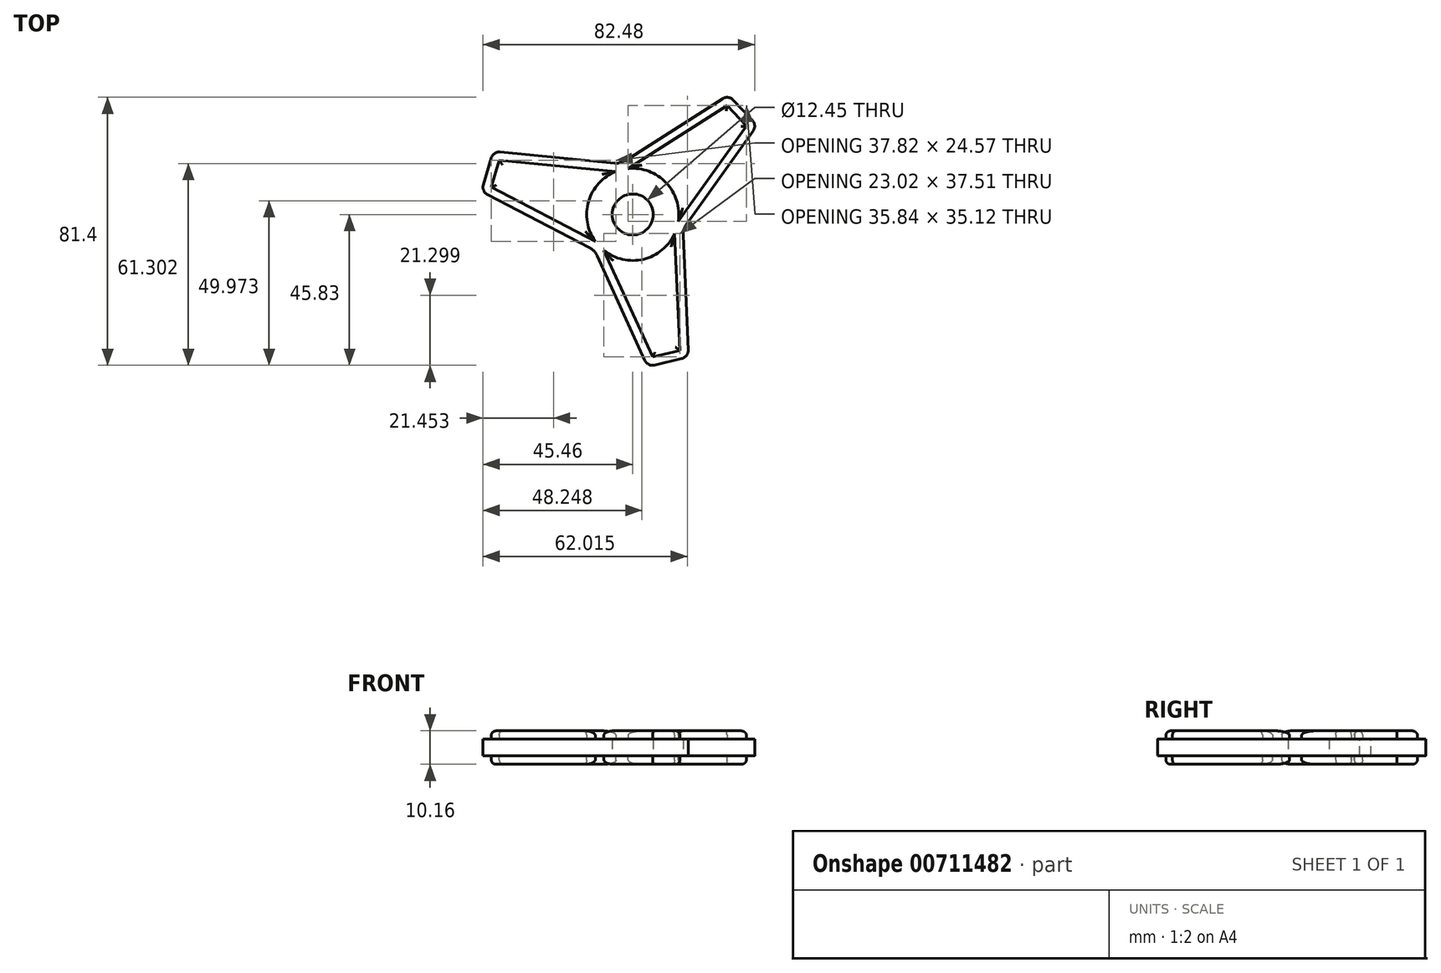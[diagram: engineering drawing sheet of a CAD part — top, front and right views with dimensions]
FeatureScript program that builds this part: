
annotation { "Feature Type Name" : "Feature", "Feature Type Description" : "" }
export const myFeature = defineFeature(function(context is Context, id is Id, definition is map)
    precondition{}
    {
        {
            var Q0;
            Q0=qCreatedBy(makeId("Top.planeOp"),FACE);
            var sketch = newSketch(context, id + "F0", { "sketchPlane" : qUnion([Q0])});
            skCircle(sketch, "E0", {"center": v(0, 0) * mm, "radius": 6.22 * mm});
            skCircle(sketch, "E1", {"center": v(0, 0) * mm, "radius": 15.88 * mm});
            skCircle(sketch, "E2.cCircle", {"center": v(0, 0) * mm, "radius": 15.88 * mm, "construction": true});
            skLineSegment(sketch, "E2.0", {"start": v(-11.51, -10.93) * mm, "end": v(-3.7, 15.44) * mm});
            skLineSegment(sketch, "E2.1", {"start": v(-3.7, 15.44) * mm, "end": v(15.22, -4.5) * mm});
            skLineSegment(sketch, "E2.2", {"start": v(15.22, -4.5) * mm, "end": v(-11.51, -10.93) * mm});
            skLineSegment(sketch, "E3", {"start": v(15.22, -4.5) * mm, "end": v(1.85, -7.72) * mm});
            skLineSegment(sketch, "E4", {"start": v(1.85, -7.72) * mm, "end": v(10.75, -44.76) * mm});
            skLineSegment(sketch, "E5", {"start": v(10.75, -44.76) * mm, "end": v(16.93, -43.28) * mm});
            skLineSegment(sketch, "E6", {"start": v(16.93, -43.28) * mm, "end": v(4.58, -46.25) * mm});
            skLineSegment(sketch, "E7", {"start": v(16.93, -43.28) * mm, "end": v(15.22, -4.5) * mm});
            skLineSegment(sketch, "E8", {"start": v(-11.51, -10.93) * mm, "end": v(4.58, -46.25) * mm});
            skLineSegment(sketch, "E9", {"start": v(15.22, -4.5) * mm, "end": v(5.76, 5.46) * mm});
            skLineSegment(sketch, "E10", {"start": v(5.76, 5.46) * mm, "end": v(33.39, 31.7) * mm});
            skLineSegment(sketch, "E11", {"start": v(33.39, 31.7) * mm, "end": v(29.02, 36.3) * mm});
            skLineSegment(sketch, "E12", {"start": v(33.39, 31.7) * mm, "end": v(37.76, 27.09) * mm});
            skLineSegment(sketch, "E13", {"start": v(37.76, 27.09) * mm, "end": v(15.22, -4.5) * mm});
            skLineSegment(sketch, "E14", {"start": v(-3.7, 15.44) * mm, "end": v(29.02, 36.3) * mm});
            skLineSegment(sketch, "E15", {"start": v(-7.61, 2.25) * mm, "end": v(-44.14, 13.07) * mm});
            skLineSegment(sketch, "E16", {"start": v(-44.14, 13.07) * mm, "end": v(-42.34, 19.16) * mm});
            skLineSegment(sketch, "E17", {"start": v(-44.14, 13.07) * mm, "end": v(-45.95, 6.98) * mm});
            skLineSegment(sketch, "E18", {"start": v(-11.51, -10.93) * mm, "end": v(-45.95, 6.98) * mm});
            skLineSegment(sketch, "E19", {"start": v(-42.34, 19.16) * mm, "end": v(-3.7, 15.44) * mm});
            skSolve(sketch);
        }
        {
            var Q0;
            {var subQ4=sQuery(id+"F0.wireOp",EDGE,"E17");Q0=makeQuery(id+"F0.imprint","IMPRINT",FACE,{"disambiguationData":[TD([[makeQuery(id+"F0.imprint","IMPRINT",EDGE,{"derivedFrom":subQ4}),1.0]])]});}
            var Q1;
            {var subQ4=sQuery(id+"F0.wireOp",EDGE,"E16");Q1=makeQuery(id+"F0.imprint","IMPRINT",FACE,{"disambiguationData":[TD([[makeQuery(id+"F0.imprint","IMPRINT",EDGE,{"derivedFrom":subQ4}),-1.0]])]});}
            var Q2;
            {var subQ0=sQuery(id+"F0.wireOp",EDGE,"E2.0");var subQ3=sQuery(id+"F0.wireOp",EDGE,"E15");var subQ5=makeQuery(id+"F0.imprint","INTERSECT",VERTEX,{"derivedFrom":[subQ0,subQ3]});Q2=makeQuery(id+"F0.imprint","IMPRINT",FACE,{"disambiguationData":[TD([[makeQuery(id+"F0.imprint","IMPRINT",EDGE,{"disambiguationData":[TD([[subQ5,-1.0]])],"derivedFrom":subQ3}),1.0]])]});}
            var Q3;
            {var subQ0=sQuery(id+"F0.wireOp",EDGE,"E2.0");var subQ3=sQuery(id+"F0.wireOp",EDGE,"E15");var subQ5=makeQuery(id+"F0.imprint","INTERSECT",VERTEX,{"derivedFrom":[subQ0,subQ3]});Q3=makeQuery(id+"F0.imprint","IMPRINT",FACE,{"disambiguationData":[TD([[makeQuery(id+"F0.imprint","IMPRINT",EDGE,{"disambiguationData":[TD([[subQ5,-1.0]])],"derivedFrom":subQ3}),-1.0]])]});}
            var Q4;
            Q4=makeQuery(id+"F0.imprint","IMPRINT",FACE,{"disambiguationData":[TD([[makeQuery(id+"F0.imprint","IMPRINT",EDGE,{"derivedFrom":sQuery(id+"F0.wireOp",EDGE,"E0")}),-1.0]])]});
            var Q5;
            {var subQ0=sQuery(id+"F0.wireOp",EDGE,"E2.1");Q5=makeQuery(id+"F0.imprint","IMPRINT",FACE,{"disambiguationData":[TD([[makeQuery(id+"F0.imprint","IMPRINT",EDGE,{"derivedFrom":subQ0}),1.0]])]});}
            var Q6;
            {var subQ4=sQuery(id+"F0.wireOp",EDGE,"E12");Q6=makeQuery(id+"F0.imprint","IMPRINT",FACE,{"disambiguationData":[TD([[makeQuery(id+"F0.imprint","IMPRINT",EDGE,{"derivedFrom":subQ4}),-1.0]])]});}
            var Q7;
            {var subQ4=sQuery(id+"F0.wireOp",EDGE,"E11");Q7=makeQuery(id+"F0.imprint","IMPRINT",FACE,{"disambiguationData":[TD([[makeQuery(id+"F0.imprint","IMPRINT",EDGE,{"derivedFrom":subQ4}),1.0]])]});}
            var Q8;
            {var subQ0=sQuery(id+"F0.wireOp",EDGE,"E3");Q8=makeQuery(id+"F0.imprint","IMPRINT",FACE,{"disambiguationData":[TD([[makeQuery(id+"F0.imprint","IMPRINT",EDGE,{"derivedFrom":subQ0}),1.0]])]});}
            var Q9;
            {var subQ0=sQuery(id+"F0.wireOp",EDGE,"E2.2");Q9=makeQuery(id+"F0.imprint","IMPRINT",FACE,{"disambiguationData":[TD([[makeQuery(id+"F0.imprint","IMPRINT",EDGE,{"derivedFrom":subQ0}),1.0]])]});}
            var Q10;
            {var subQ0=sQuery(id+"F0.wireOp",EDGE,"E8");Q10=makeQuery(id+"F0.imprint","IMPRINT",FACE,{"disambiguationData":[TD([[makeQuery(id+"F0.imprint","IMPRINT",EDGE,{"derivedFrom":subQ0}),1.0]])]});}
            var Q11;
            {var subQ0=sQuery(id+"F0.wireOp",EDGE,"E7");Q11=makeQuery(id+"F0.imprint","IMPRINT",FACE,{"disambiguationData":[TD([[makeQuery(id+"F0.imprint","IMPRINT",EDGE,{"derivedFrom":subQ0}),1.0]])]});}
            var Q12;
            {var subQ0=sQuery(id+"F0.wireOp",EDGE,"E9");Q12=makeQuery(id+"F0.imprint","IMPRINT",FACE,{"disambiguationData":[TD([[makeQuery(id+"F0.imprint","IMPRINT",EDGE,{"derivedFrom":subQ0}),-1.0]])]});}
            extrude(context, id + "F1", {"entities" : qUnion([Q0, Q1, Q2, Q3, Q4, Q5, Q6, Q7, Q8, Q9, Q10, Q11, Q12]), "depth" : 5.08 * mm, "offsetDistance" : 25.4 * mm});
        }
        {
            var Q0;
            Q0=makeQuery(id+"F1.opExtrude","SWEPT_EDGE",EDGE,{"disambiguationData":[OSD([sQuery(id+"F0.wireOp",EDGE,"E17"),sQuery(id+"F0.wireOp",EDGE,"E18")])]});
            var Q1;
            Q1=makeQuery(id+"F1.opExtrude","SWEPT_EDGE",EDGE,{"disambiguationData":[OSD([sQuery(id+"F0.wireOp",EDGE,"E16"),sQuery(id+"F0.wireOp",EDGE,"E19")])]});
            var Q2;
            Q2=makeQuery(id+"F1.opExtrude","SWEPT_EDGE",EDGE,{"disambiguationData":[OSD([sQuery(id+"F0.wireOp",EDGE,"E11"),sQuery(id+"F0.wireOp",EDGE,"E14")])]});
            var Q3;
            Q3=makeQuery(id+"F1.opExtrude","SWEPT_EDGE",EDGE,{"disambiguationData":[OSD([sQuery(id+"F0.wireOp",EDGE,"E12"),sQuery(id+"F0.wireOp",EDGE,"E13")])]});
            var Q4;
            Q4=makeQuery(id+"F1.opExtrude","SWEPT_EDGE",EDGE,{"disambiguationData":[OSD([sQuery(id+"F0.wireOp",EDGE,"E6"),sQuery(id+"F0.wireOp",EDGE,"E7")])]});
            var Q5;
            Q5=makeQuery(id+"F1.opExtrude","SWEPT_EDGE",EDGE,{"disambiguationData":[OSD([sQuery(id+"F0.wireOp",EDGE,"E6"),sQuery(id+"F0.wireOp",EDGE,"E8")])]});
            fillet(context, id + "F2", {"entities" : qUnion([Q0, Q1, Q2, Q3, Q4, Q5]), "radius" : 2.54 * mm, "tangentPropagation" : true, "allowEdgeOverflow" : false});
        }
        {
            var Q0;
            Q0=makeQuery(id+"F1.opExtrude","SWEPT_EDGE",EDGE,{"disambiguationData":[OSD([sQuery(id+"F0.wireOp",EDGE,"E1"),sQuery(id+"F0.wireOp",EDGE,"E2.0"),sQuery(id+"F0.wireOp",EDGE,"E2.2"),sQuery(id+"F0.wireOp",EDGE,"E8"),sQuery(id+"F0.wireOp",EDGE,"E18")])]});
            var Q1;
            Q1=makeQuery(id+"F1.opExtrude","SWEPT_EDGE",EDGE,{"disambiguationData":[OSD([sQuery(id+"F0.wireOp",EDGE,"E1"),sQuery(id+"F0.wireOp",EDGE,"E2.0"),sQuery(id+"F0.wireOp",EDGE,"E2.1"),sQuery(id+"F0.wireOp",EDGE,"E14"),sQuery(id+"F0.wireOp",EDGE,"E19")])]});
            var Q2;
            Q2=makeQuery(id+"F1.opExtrude","SWEPT_EDGE",EDGE,{"disambiguationData":[OSD([sQuery(id+"F0.wireOp",EDGE,"E1"),sQuery(id+"F0.wireOp",EDGE,"E3"),sQuery(id+"F0.wireOp",EDGE,"E7"),sQuery(id+"F0.wireOp",EDGE,"E9"),sQuery(id+"F0.wireOp",EDGE,"E13")])]});
            fillet(context, id + "F3", {"entities" : qUnion([Q0, Q1, Q2]), "radius" : 5.08 * mm, "tangentPropagation" : true, "allowEdgeOverflow" : false});
        }
        {
            var Q0;
            Q0=makeQuery(id+"F1.opExtrude","CAP_FACE",FACE,{"disambiguationData":[OSD([sQuery(id+"F0.wireOp",EDGE,"E0"),sQuery(id+"F0.wireOp",EDGE,"E6"),sQuery(id+"F0.wireOp",EDGE,"E7"),sQuery(id+"F0.wireOp",EDGE,"E8"),sQuery(id+"F0.wireOp",EDGE,"E11"),sQuery(id+"F0.wireOp",EDGE,"E12"),sQuery(id+"F0.wireOp",EDGE,"E13"),sQuery(id+"F0.wireOp",EDGE,"E14"),sQuery(id+"F0.wireOp",EDGE,"E16"),sQuery(id+"F0.wireOp",EDGE,"E17"),sQuery(id+"F0.wireOp",EDGE,"E18"),sQuery(id+"F0.wireOp",EDGE,"E19")])],"isStart":false});
            var sketch = newSketch(context, id + "F4", { "sketchPlane" : qUnion([Q0])});
            skLineSegment(sketch, "E20", {"start": v(-40.5, 16.43) * mm, "end": v(-42.92, 8.27) * mm});
            skLineSegment(sketch, "E21", {"start": v(-40.5, 16.43) * mm, "end": v(-5.1, 13.02) * mm});
            skLineSegment(sketch, "E22", {"start": v(-42.92, 8.27) * mm, "end": v(-11.37, -8.14) * mm});
            skLineSegment(sketch, "E23", {"start": v(-11.37, -8.14) * mm, "end": v(-5.1, 13.02) * mm});
            skLineSegment(sketch, "E24", {"start": v(14.3, -41.3) * mm, "end": v(6.02, -43.29) * mm});
            skLineSegment(sketch, "E25", {"start": v(6.02, -43.29) * mm, "end": v(-8.72, -10.93) * mm});
            skLineSegment(sketch, "E26", {"start": v(14.3, -41.3) * mm, "end": v(12.74, -5.77) * mm});
            skLineSegment(sketch, "E27", {"start": v(12.74, -5.77) * mm, "end": v(-8.72, -10.93) * mm});
            skLineSegment(sketch, "E28", {"start": v(28.62, 33.03) * mm, "end": v(34.48, 26.86) * mm});
            skLineSegment(sketch, "E29", {"start": v(34.48, 26.86) * mm, "end": v(13.83, -2.09) * mm});
            skLineSegment(sketch, "E30", {"start": v(28.62, 33.03) * mm, "end": v(-1.37, 13.92) * mm});
            skLineSegment(sketch, "E31", {"start": v(-1.37, 13.92) * mm, "end": v(13.83, -2.09) * mm});
            skCircle(sketch, "E32", {"center": v(0, 0) * mm, "radius": 13.98 * mm});
            skSolve(sketch);
        }
        {
            var Q0;
            Q0=makeQuery(id+"F4.imprint","IMPRINT",FACE,{"disambiguationData":[TD([[makeQuery(id+"F4.imprint","IMPRINT",EDGE,{"derivedFrom":sQuery(id+"F4.wireOp",EDGE,"E24")}),-1.0]])]});
            var Q1;
            Q1=makeQuery(id+"F4.imprint","IMPRINT",FACE,{"disambiguationData":[TD([[makeQuery(id+"F4.imprint","IMPRINT",EDGE,{"derivedFrom":sQuery(id+"F4.wireOp",EDGE,"E20")}),1.0]])]});
            var Q2;
            Q2=makeQuery(id+"F4.imprint","IMPRINT",FACE,{"disambiguationData":[TD([[makeQuery(id+"F4.imprint","IMPRINT",EDGE,{"derivedFrom":sQuery(id+"F4.wireOp",EDGE,"E28")}),-1.0]])]});
            extrude(context, id + "F5", {"entities" : qUnion([Q0, Q1, Q2]), "operationType" : NewBodyOperationType.ADD, "depth" : 2.54 * mm, "offsetDistance" : 25.4 * mm});
        }
        {
            var Q0;
            Q0=makeQuery(id+"F1.opExtrude","CAP_FACE",FACE,{"disambiguationData":[OSD([sQuery(id+"F0.wireOp",EDGE,"E0"),sQuery(id+"F0.wireOp",EDGE,"E6"),sQuery(id+"F0.wireOp",EDGE,"E7"),sQuery(id+"F0.wireOp",EDGE,"E8"),sQuery(id+"F0.wireOp",EDGE,"E11"),sQuery(id+"F0.wireOp",EDGE,"E12"),sQuery(id+"F0.wireOp",EDGE,"E13"),sQuery(id+"F0.wireOp",EDGE,"E14"),sQuery(id+"F0.wireOp",EDGE,"E16"),sQuery(id+"F0.wireOp",EDGE,"E17"),sQuery(id+"F0.wireOp",EDGE,"E18"),sQuery(id+"F0.wireOp",EDGE,"E19")])],"isStart":true});
            var sketch = newSketch(context, id + "F6", { "sketchPlane" : qUnion([Q0])});
            skLineSegment(sketch, "E33", {"start": v(6.02, 43.29) * mm, "end": v(14.3, 41.3) * mm});
            skLineSegment(sketch, "E34", {"start": v(14.3, 41.3) * mm, "end": v(12.74, 5.77) * mm});
            skLineSegment(sketch, "E35", {"start": v(6.02, 43.29) * mm, "end": v(-8.72, 10.93) * mm});
            skLineSegment(sketch, "E36", {"start": v(-42.92, -8.27) * mm, "end": v(-40.5, -16.43) * mm});
            skLineSegment(sketch, "E37", {"start": v(-40.5, -16.43) * mm, "end": v(-5.1, -13.09) * mm});
            skLineSegment(sketch, "E38", {"start": v(-42.92, -8.27) * mm, "end": v(-11.37, 8.14) * mm});
            skLineSegment(sketch, "E39", {"start": v(34.48, -26.86) * mm, "end": v(28.62, -33.03) * mm});
            skLineSegment(sketch, "E40", {"start": v(28.62, -33.03) * mm, "end": v(-1.37, -13.92) * mm});
            skLineSegment(sketch, "E41", {"start": v(34.48, -26.86) * mm, "end": v(13.83, 2.09) * mm});
            skCircle(sketch, "E42", {"center": v(0, 0) * mm, "radius": 13.98 * mm});
            skLineSegment(sketch, "E43", {"start": v(-11.37, 8.14) * mm, "end": v(-5.1, -13.09) * mm});
            skLineSegment(sketch, "E44", {"start": v(-1.37, -13.92) * mm, "end": v(13.83, 2.09) * mm});
            skLineSegment(sketch, "E45", {"start": v(12.74, 5.77) * mm, "end": v(-8.72, 10.93) * mm});
            skSolve(sketch);
        }
        {
            var Q0;
            Q0=makeQuery(id+"F6.imprint","IMPRINT",FACE,{"disambiguationData":[TD([[makeQuery(id+"F6.imprint","IMPRINT",EDGE,{"derivedFrom":sQuery(id+"F6.wireOp",EDGE,"E33")}),-1.0]])]});
            var Q1;
            Q1=makeQuery(id+"F6.imprint","IMPRINT",FACE,{"disambiguationData":[TD([[makeQuery(id+"F6.imprint","IMPRINT",EDGE,{"derivedFrom":sQuery(id+"F6.wireOp",EDGE,"E36")}),1.0]])]});
            var Q2;
            Q2=makeQuery(id+"F6.imprint","IMPRINT",FACE,{"disambiguationData":[TD([[makeQuery(id+"F6.imprint","IMPRINT",EDGE,{"derivedFrom":sQuery(id+"F6.wireOp",EDGE,"E39")}),-1.0]])]});
            extrude(context, id + "F7", {"entities" : qUnion([Q0, Q1, Q2]), "operationType" : NewBodyOperationType.ADD, "depth" : 2.54 * mm, "offsetDistance" : 25.4 * mm});
        }
        {
            var Q0;
            Q0=makeQuery(id+"F7.opExtrude","CAP_EDGE",EDGE,{"disambiguationData":[OSD([sQuery(id+"F6.wireOp",EDGE,"E37")])],"isStart":false});
            var Q1;
            Q1=makeQuery(id+"F7.opExtrude","CAP_EDGE",EDGE,{"disambiguationData":[OSD([sQuery(id+"F6.wireOp",EDGE,"E36")])],"isStart":false});
            var Q2;
            Q2=makeQuery(id+"F7.opExtrude","CAP_EDGE",EDGE,{"disambiguationData":[OSD([sQuery(id+"F6.wireOp",EDGE,"E38")])],"isStart":false});
            var Q3;
            {var subQ0=sQuery(id+"F6.wireOp",EDGE,"E43");var subQ1=sQuery(id+"F6.wireOp",EDGE,"E42");Q3=makeQuery(id+"F7.opExtrude","CAP_EDGE",EDGE,{"disambiguationData":[OSD([subQ1]),TDD([makeQuery(id+"F6.imprint","IMPRINT",EDGE,{"disambiguationData":[TD([[makeQuery(id+"F6.imprint","INTERSECT",VERTEX,{"derivedFrom":[subQ1,subQ0]}),1.0]])],"derivedFrom":subQ1})])],"isStart":false});}
            var Q4;
            Q4=makeQuery(id+"F7.opExtrude","CAP_FACE",FACE,{"disambiguationData":[OSD([sQuery(id+"F6.wireOp",EDGE,"E39"),sQuery(id+"F6.wireOp",EDGE,"E40"),sQuery(id+"F6.wireOp",EDGE,"E41"),sQuery(id+"F6.wireOp",EDGE,"E42")])],"isStart":false});
            var Q5;
            Q5=makeQuery(id+"F7.opExtrude","CAP_FACE",FACE,{"disambiguationData":[OSD([sQuery(id+"F6.wireOp",EDGE,"E33"),sQuery(id+"F6.wireOp",EDGE,"E34"),sQuery(id+"F6.wireOp",EDGE,"E35"),sQuery(id+"F6.wireOp",EDGE,"E42")])],"isStart":false});
            var Q6;
            Q6=makeQuery(id+"F5.opExtrude","CAP_FACE",FACE,{"disambiguationData":[OSD([sQuery(id+"F4.wireOp",EDGE,"E20"),sQuery(id+"F4.wireOp",EDGE,"E21"),sQuery(id+"F4.wireOp",EDGE,"E22"),sQuery(id+"F4.wireOp",EDGE,"E32")])],"isStart":false});
            var Q7;
            Q7=makeQuery(id+"F5.opExtrude","CAP_FACE",FACE,{"disambiguationData":[OSD([sQuery(id+"F4.wireOp",EDGE,"E28"),sQuery(id+"F4.wireOp",EDGE,"E29"),sQuery(id+"F4.wireOp",EDGE,"E30"),sQuery(id+"F4.wireOp",EDGE,"E32")])],"isStart":false});
            var Q8;
            Q8=makeQuery(id+"F5.opExtrude","CAP_FACE",FACE,{"disambiguationData":[OSD([sQuery(id+"F4.wireOp",EDGE,"E24"),sQuery(id+"F4.wireOp",EDGE,"E25"),sQuery(id+"F4.wireOp",EDGE,"E26"),sQuery(id+"F4.wireOp",EDGE,"E32")])],"isStart":false});
            fillet(context, id + "F8", {"entities" : qUnion([Q0, Q1, Q2, Q3, Q4, Q5, Q6, Q7, Q8]), "radius" : 1.27 * mm, "tangentPropagation" : true, "allowEdgeOverflow" : false});
        }
    });
